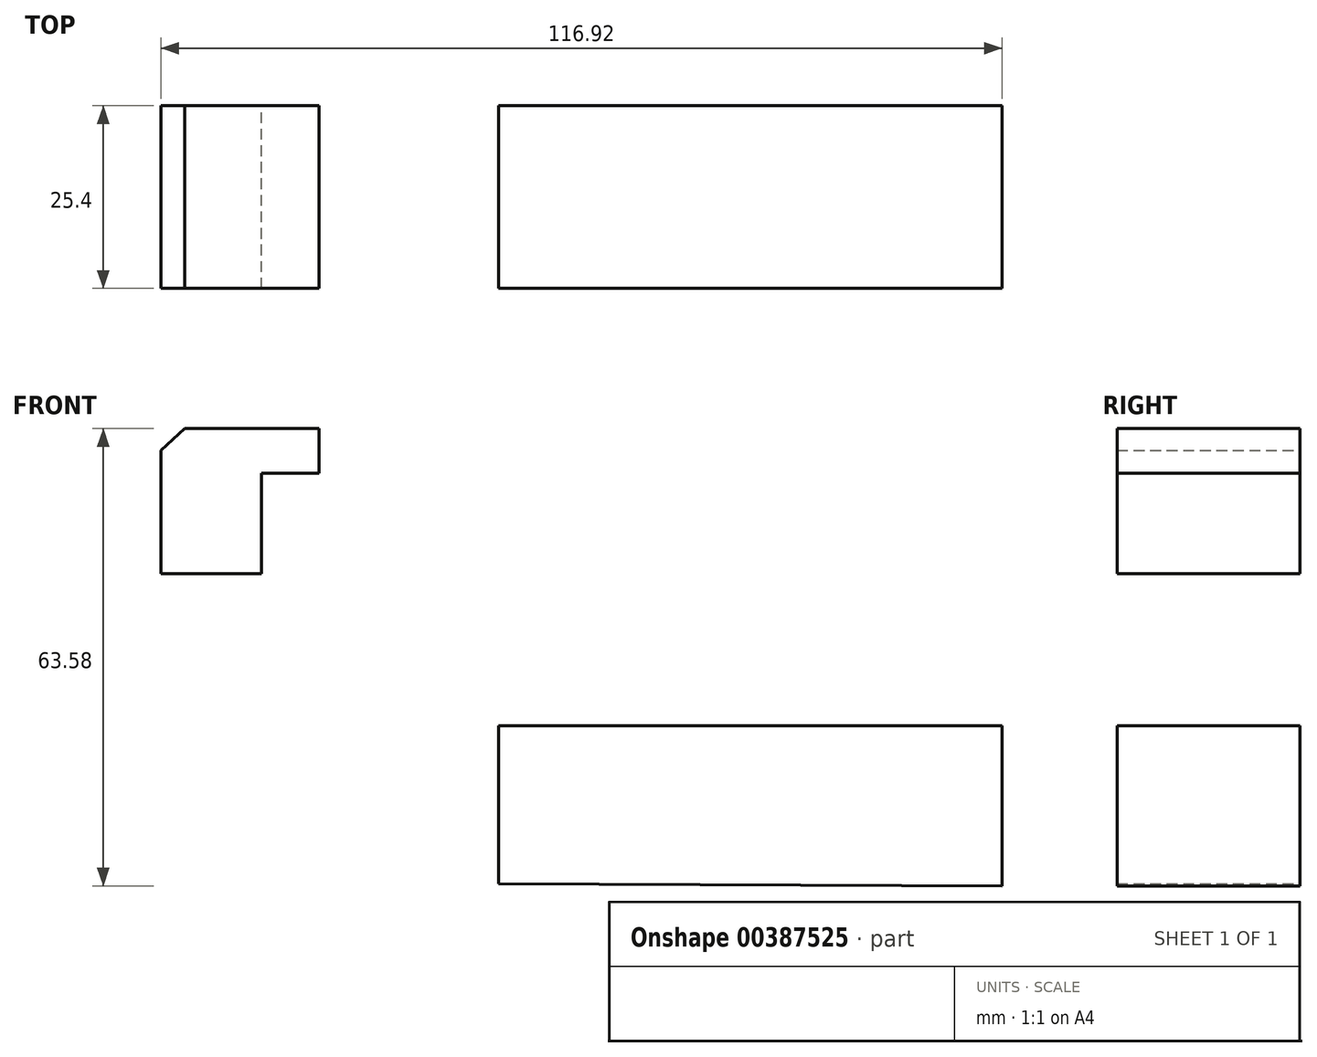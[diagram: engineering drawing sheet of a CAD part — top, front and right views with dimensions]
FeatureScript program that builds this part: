
annotation { "Feature Type Name" : "Feature", "Feature Type Description" : "" }
export const myFeature = defineFeature(function(context is Context, id is Id, definition is map)
    precondition{}
    {
        {
            var Q0;
            Q0=qCreatedBy(makeId("Front.planeOp"),FACE);
            var sketch = newSketch(context, id + "F0", { "sketchPlane" : qUnion([Q0])});
            skLineSegment(sketch, "E0", {"start": v(-59.72, 22.93) * mm, "end": v(-59.72, 5.76) * mm});
            skLineSegment(sketch, "E1", {"start": v(-59.72, 5.76) * mm, "end": v(-45.73, 5.76) * mm});
            skLineSegment(sketch, "E2", {"start": v(-45.73, 5.76) * mm, "end": v(-45.73, 19.75) * mm});
            skLineSegment(sketch, "E3", {"start": v(-59.72, 22.93) * mm, "end": v(-56.4, 25.94) * mm});
            skLineSegment(sketch, "E4", {"start": v(-56.4, 25.94) * mm, "end": v(-37.73, 25.94) * mm});
            skLineSegment(sketch, "E5", {"start": v(-45.73, 19.75) * mm, "end": v(-37.73, 19.75) * mm});
            skLineSegment(sketch, "E6", {"start": v(-37.73, 25.94) * mm, "end": v(-37.73, 19.75) * mm});
            skLineSegment(sketch, "E7", {"start": v(-12.8, -15.34) * mm, "end": v(-12.8, -37.34) * mm});
            skLineSegment(sketch, "E8", {"start": v(-12.8, -15.34) * mm, "end": v(57.2, -15.34) * mm});
            skLineSegment(sketch, "E9", {"start": v(57.2, -15.34) * mm, "end": v(57.2, -37.64) * mm});
            skLineSegment(sketch, "E10", {"start": v(-12.8, -37.34) * mm, "end": v(57.2, -37.64) * mm});
            skLineSegment(sketch, "E11", {"start": v(-12.8, -23.34) * mm, "end": v(57.2, -23.34) * mm});
            skSolve(sketch);
        }
        {
            var Q0;
            Q0 = qSketchRegion(id + "F0", true);
            extrude(context, id + "F1", {"entities" : qUnion([Q0]), "depth" : 25.4 * mm});
        }
    });
